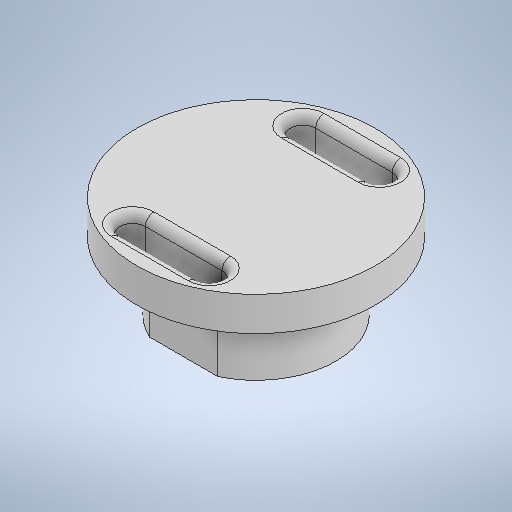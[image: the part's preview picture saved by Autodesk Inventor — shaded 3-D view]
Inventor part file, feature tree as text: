
AUTODESK INVENTOR PART (.ipt)
format: ipt  version: 2025.2 (Build 292293000, 293)  size: 268,288 bytes
history: native  units: in
note: dims shown in document units (in); Inventor stores cm internally (conversion verified against a paired STEP export)
features: extrude x3, sketch x3, fillet x1
ambient origin geometry x8: Origin, YZ Plane, XZ Plane, XY Plane, X Axis, Y Axis, Z Axis, Center Point
bodies: Solid1 (feature_tree)
feature tree (7):
  extrude  "Extrusion1"  Depth=0.4in TaperAngle=0.0deg
  extrude  "Extrusion2"  Depth=0.2in TaperAngle=0.0deg
  extrude  "Extrusion3"  Depth=0.05in
  fillet  "Fillet1"  Radius=0.15in
  sketch  "Sketch1"  dims[d0=0.94in d1=0.4in d2=0.0in]
  sketch  "Sketch2"  dims[d3=1.4in d4=0.2in d5=0.0in]
  sketch  "Sketch3"  dims[d6=0.0in d7=0.3in d8=0.15in d9=0.15in d10=0.5in d11=0.3in d12=0.3in d13=0.5in d14=0.6in d15=0.0in d16=0.05in]
